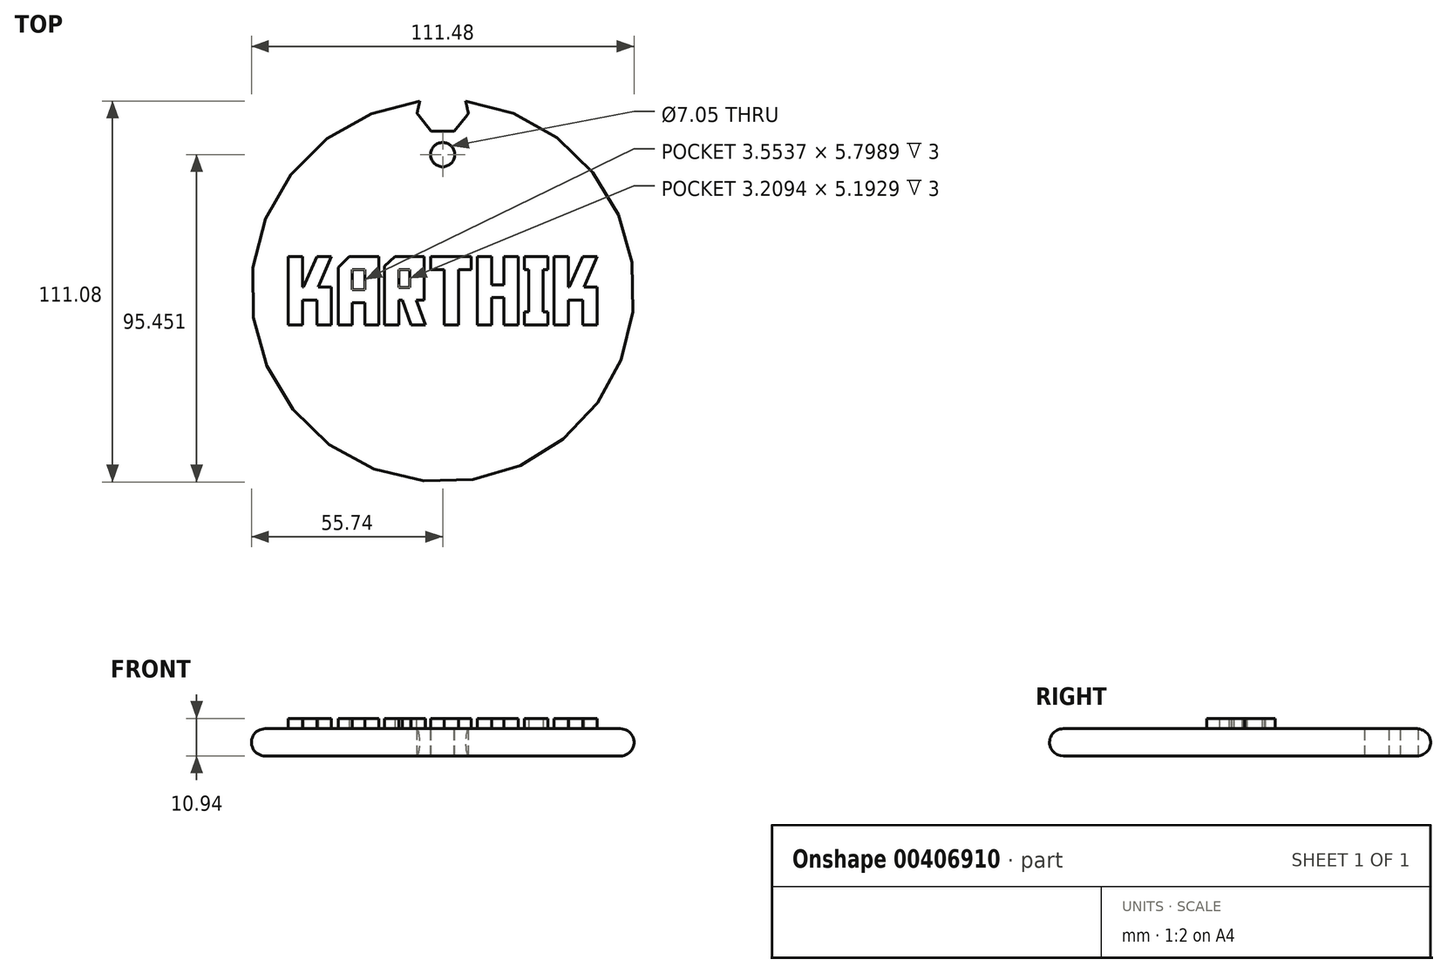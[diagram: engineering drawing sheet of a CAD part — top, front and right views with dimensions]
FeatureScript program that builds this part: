
annotation { "Feature Type Name" : "Feature", "Feature Type Description" : "" }
export const myFeature = defineFeature(function(context is Context, id is Id, definition is map)
    precondition{}
    {
        {
            var Q0;
            Q0=qCreatedBy(makeId("Front.planeOp"),FACE);
            var sketch = newSketch(context, id + "F0", { "sketchPlane" : qUnion([Q0])});
            skLineSegment(sketch, "E0.bottom", {"start": v(0, 0) * mm, "end": v(-51.77, 0) * mm});
            skLineSegment(sketch, "E0.top", {"start": v(0, 7.94) * mm, "end": v(-51.77, 7.94) * mm});
            skLineSegment(sketch, "E0.left", {"start": v(0, 0) * mm, "end": v(0, 7.94) * mm});
            skLineSegment(sketch, "E0.right", {"start": v(-51.77, 0) * mm, "end": v(-51.77, 7.94) * mm});
            skArc(sketch, "E1", {"start": v(-51.77, 7.94) * mm, "mid": v(-55.74, 3.97) * mm, "end": v(-51.77, 0) * mm});
            skSolve(sketch);
        }
        {
            var Q0;
            Q0 = qSketchRegion(id + "F0", true);
            var Q1;
            Q1=sQuery(id+"F0.wireOp",EDGE,"E0.left");
            revolve(context, id + "F1", {"entities" : qUnion([Q0]), "axis" : qUnion([Q1]), "revolveType" : RevolveType.FULL});
        }
        {
            var Q0;
            Q0=makeQuery(id+"F1.opRevolve","SWEPT_FACE",FACE,{"disambiguationData":[OSD([sQuery(id+"F0.wireOp",EDGE,"E0.top")])]});
            var sketch = newSketch(context, id + "F2", { "sketchPlane" : qUnion([Q0])});
            skLineSegment(sketch, "E2", {"start": v(-32.45, 1.07) * mm, "end": v(-32.45, -9.96) * mm});
            skLineSegment(sketch, "E3", {"start": v(-32.45, -9.96) * mm, "end": v(-36.63, -9.96) * mm});
            skLineSegment(sketch, "E4", {"start": v(-36.63, -9.96) * mm, "end": v(-36.63, -2.69) * mm});
            skLineSegment(sketch, "E5", {"start": v(-36.63, -2.69) * mm, "end": v(-40.83, -2.69) * mm});
            skLineSegment(sketch, "E6", {"start": v(-40.83, -2.69) * mm, "end": v(-40.83, -9.96) * mm});
            skLineSegment(sketch, "E7", {"start": v(-40.83, -9.96) * mm, "end": v(-45, -9.96) * mm});
            skLineSegment(sketch, "E8", {"start": v(-45, -9.96) * mm, "end": v(-45, 9.96) * mm});
            skLineSegment(sketch, "E9", {"start": v(-45, 9.96) * mm, "end": v(-40.83, 9.96) * mm});
            skLineSegment(sketch, "E10", {"start": v(-40.83, 9.96) * mm, "end": v(-40.83, 1.07) * mm});
            skLineSegment(sketch, "E11", {"start": v(-40.83, 1.07) * mm, "end": v(-40.55, 1.07) * mm});
            skLineSegment(sketch, "E12", {"start": v(-40.55, 1.07) * mm, "end": v(-36.64, 9.96) * mm});
            skLineSegment(sketch, "E13", {"start": v(-36.64, 9.96) * mm, "end": v(-32.48, 9.96) * mm});
            skLineSegment(sketch, "E14", {"start": v(-32.48, 9.96) * mm, "end": v(-36.3, 1.07) * mm});
            skLineSegment(sketch, "E15", {"start": v(-36.3, 1.07) * mm, "end": v(-32.45, 1.07) * mm});
            skLineSegment(sketch, "E16", {"start": v(-26.3, -9.96) * mm, "end": v(-30.5, -9.96) * mm});
            skLineSegment(sketch, "E17", {"start": v(-30.5, -9.96) * mm, "end": v(-30.5, 6.8) * mm});
            skLineSegment(sketch, "E18", {"start": v(-30.5, 6.8) * mm, "end": v(-27.29, 9.96) * mm});
            skLineSegment(sketch, "E19", {"start": v(-27.29, 9.96) * mm, "end": v(-18.58, 9.96) * mm});
            skLineSegment(sketch, "E20", {"start": v(-18.58, 9.96) * mm, "end": v(-18.58, -9.96) * mm});
            skLineSegment(sketch, "E21", {"start": v(-18.58, -9.96) * mm, "end": v(-22.75, -9.96) * mm});
            skLineSegment(sketch, "E22", {"start": v(-22.75, -9.96) * mm, "end": v(-22.75, -3.42) * mm});
            skLineSegment(sketch, "E23", {"start": v(-22.75, -3.42) * mm, "end": v(-26.3, -3.42) * mm});
            skLineSegment(sketch, "E24", {"start": v(-26.3, -3.42) * mm, "end": v(-26.3, -9.96) * mm});
            skLineSegment(sketch, "E25", {"start": v(-22.75, 0.37) * mm, "end": v(-22.75, 6.17) * mm});
            skLineSegment(sketch, "E26", {"start": v(-22.75, 6.17) * mm, "end": v(-26.3, 6.17) * mm});
            skLineSegment(sketch, "E27", {"start": v(-26.3, 6.17) * mm, "end": v(-26.3, 0.37) * mm});
            skLineSegment(sketch, "E28", {"start": v(-26.3, 0.37) * mm, "end": v(-22.75, 0.37) * mm});
            skLineSegment(sketch, "E29", {"start": v(-9.26, -9.96) * mm, "end": v(-11.74, -2.75) * mm});
            skLineSegment(sketch, "E30", {"start": v(-11.74, -2.75) * mm, "end": v(-12.84, -2.75) * mm});
            skLineSegment(sketch, "E31", {"start": v(-12.84, -2.75) * mm, "end": v(-12.84, -9.96) * mm});
            skLineSegment(sketch, "E32", {"start": v(-12.84, -9.96) * mm, "end": v(-17.01, -9.96) * mm});
            skLineSegment(sketch, "E33", {"start": v(-17.01, -9.96) * mm, "end": v(-17.01, 7.15) * mm});
            skLineSegment(sketch, "E34", {"start": v(-17.01, 7.15) * mm, "end": v(-13.98, 9.96) * mm});
            skLineSegment(sketch, "E35", {"start": v(-13.98, 9.96) * mm, "end": v(-5.45, 9.96) * mm});
            skLineSegment(sketch, "E36", {"start": v(-5.45, 9.96) * mm, "end": v(-5.45, -2.7) * mm});
            skLineSegment(sketch, "E37", {"start": v(-5.45, -2.7) * mm, "end": v(-7.71, -2.7) * mm});
            skLineSegment(sketch, "E38", {"start": v(-7.71, -2.7) * mm, "end": v(-5.07, -9.96) * mm});
            skLineSegment(sketch, "E39", {"start": v(-5.07, -9.96) * mm, "end": v(-9.26, -9.96) * mm});
            skLineSegment(sketch, "E40", {"start": v(-9.63, 0.98) * mm, "end": v(-9.63, 6.17) * mm});
            skLineSegment(sketch, "E41", {"start": v(-9.63, 6.17) * mm, "end": v(-12.84, 6.17) * mm});
            skLineSegment(sketch, "E42", {"start": v(-12.84, 6.17) * mm, "end": v(-12.84, 0.98) * mm});
            skLineSegment(sketch, "E43", {"start": v(-12.84, 0.98) * mm, "end": v(-9.63, 0.98) * mm});
            skLineSegment(sketch, "E44", {"start": v(8.33, 6.17) * mm, "end": v(4.57, 6.17) * mm});
            skLineSegment(sketch, "E45", {"start": v(4.57, 6.17) * mm, "end": v(4.57, -9.96) * mm});
            skLineSegment(sketch, "E46", {"start": v(4.57, -9.96) * mm, "end": v(0.37, -9.96) * mm});
            skLineSegment(sketch, "E47", {"start": v(0.37, -9.96) * mm, "end": v(0.37, 6.17) * mm});
            skLineSegment(sketch, "E48", {"start": v(0.37, 6.17) * mm, "end": v(-3.53, 6.17) * mm});
            skLineSegment(sketch, "E49", {"start": v(-3.53, 6.17) * mm, "end": v(-3.53, 9.96) * mm});
            skLineSegment(sketch, "E50", {"start": v(-3.53, 9.96) * mm, "end": v(8.33, 9.96) * mm});
            skLineSegment(sketch, "E51", {"start": v(8.33, 9.96) * mm, "end": v(8.33, 6.17) * mm});
            skLineSegment(sketch, "E52", {"start": v(14.2, 1.78) * mm, "end": v(17.78, 1.78) * mm});
            skLineSegment(sketch, "E53", {"start": v(17.78, 1.78) * mm, "end": v(17.78, 9.96) * mm});
            skLineSegment(sketch, "E54", {"start": v(17.78, 9.96) * mm, "end": v(21.96, 9.96) * mm});
            skLineSegment(sketch, "E55", {"start": v(21.96, 9.96) * mm, "end": v(21.96, -9.96) * mm});
            skLineSegment(sketch, "E56", {"start": v(21.96, -9.96) * mm, "end": v(17.78, -9.96) * mm});
            skLineSegment(sketch, "E57", {"start": v(17.78, -9.96) * mm, "end": v(17.78, -2) * mm});
            skLineSegment(sketch, "E58", {"start": v(17.78, -2) * mm, "end": v(14.2, -2) * mm});
            skLineSegment(sketch, "E59", {"start": v(14.2, -2) * mm, "end": v(14.2, -9.96) * mm});
            skLineSegment(sketch, "E60", {"start": v(14.2, -9.96) * mm, "end": v(10.03, -9.96) * mm});
            skLineSegment(sketch, "E61", {"start": v(10.03, -9.96) * mm, "end": v(10.03, 9.96) * mm});
            skLineSegment(sketch, "E62", {"start": v(10.03, 9.96) * mm, "end": v(14.2, 9.96) * mm});
            skLineSegment(sketch, "E63", {"start": v(14.2, 9.96) * mm, "end": v(14.2, 1.78) * mm});
            skLineSegment(sketch, "E64", {"start": v(30.66, -6.18) * mm, "end": v(30.66, -9.96) * mm});
            skLineSegment(sketch, "E65", {"start": v(30.66, -9.96) * mm, "end": v(23.73, -9.96) * mm});
            skLineSegment(sketch, "E66", {"start": v(23.73, -9.96) * mm, "end": v(23.73, -6.18) * mm});
            skLineSegment(sketch, "E67", {"start": v(23.73, -6.18) * mm, "end": v(25.11, -6.18) * mm});
            skLineSegment(sketch, "E68", {"start": v(25.11, -6.18) * mm, "end": v(25.11, 6.18) * mm});
            skLineSegment(sketch, "E69", {"start": v(25.11, 6.18) * mm, "end": v(23.73, 6.18) * mm});
            skLineSegment(sketch, "E70", {"start": v(23.73, 6.18) * mm, "end": v(23.73, 9.96) * mm});
            skLineSegment(sketch, "E71", {"start": v(23.73, 9.96) * mm, "end": v(30.66, 9.96) * mm});
            skLineSegment(sketch, "E72", {"start": v(30.66, 9.96) * mm, "end": v(30.66, 6.18) * mm});
            skLineSegment(sketch, "E73", {"start": v(30.66, 6.18) * mm, "end": v(29.28, 6.18) * mm});
            skLineSegment(sketch, "E74", {"start": v(29.28, 6.18) * mm, "end": v(29.28, -6.18) * mm});
            skLineSegment(sketch, "E75", {"start": v(29.28, -6.18) * mm, "end": v(30.66, -6.18) * mm});
            skLineSegment(sketch, "E76", {"start": v(45, 1.07) * mm, "end": v(45, -9.96) * mm});
            skLineSegment(sketch, "E77", {"start": v(45, -9.96) * mm, "end": v(40.83, -9.96) * mm});
            skLineSegment(sketch, "E78", {"start": v(40.83, -9.96) * mm, "end": v(40.83, -2.69) * mm});
            skLineSegment(sketch, "E79", {"start": v(40.83, -2.69) * mm, "end": v(36.63, -2.69) * mm});
            skLineSegment(sketch, "E80", {"start": v(36.63, -2.69) * mm, "end": v(36.63, -9.96) * mm});
            skLineSegment(sketch, "E81", {"start": v(36.63, -9.96) * mm, "end": v(32.45, -9.96) * mm});
            skLineSegment(sketch, "E82", {"start": v(32.45, -9.96) * mm, "end": v(32.45, 9.96) * mm});
            skLineSegment(sketch, "E83", {"start": v(32.45, 9.96) * mm, "end": v(36.63, 9.96) * mm});
            skLineSegment(sketch, "E84", {"start": v(36.63, 9.96) * mm, "end": v(36.63, 1.07) * mm});
            skLineSegment(sketch, "E85", {"start": v(36.63, 1.07) * mm, "end": v(36.9, 1.07) * mm});
            skLineSegment(sketch, "E86", {"start": v(36.9, 1.07) * mm, "end": v(40.81, 9.96) * mm});
            skLineSegment(sketch, "E87", {"start": v(40.81, 9.96) * mm, "end": v(44.97, 9.96) * mm});
            skLineSegment(sketch, "E88", {"start": v(44.97, 9.96) * mm, "end": v(41.16, 1.07) * mm});
            skLineSegment(sketch, "E89", {"start": v(41.16, 1.07) * mm, "end": v(45, 1.07) * mm});
            skSolve(sketch);
        }
        {
            var Q0;
            Q0=makeQuery(id+"F2.imprint","IMPRINT",FACE,{"disambiguationData":[TD([[makeQuery(id+"F2.imprint","IMPRINT",EDGE,{"derivedFrom":sQuery(id+"F2.wireOp",EDGE,"E2")}),1.0]])]});
            var sketch = newSketch(context, id + "F3", { "sketchPlane" : qUnion([Q0])});
            skCircle(sketch, "E90.cCircle", {"center": v(0, 53.46) * mm, "radius": 6.92 * mm, "construction": true});
            skLineSegment(sketch, "E90.0", {"start": v(3.33, 46.54) * mm, "end": v(-3.33, 46.54) * mm});
            skLineSegment(sketch, "E90.1", {"start": v(-3.33, 46.54) * mm, "end": v(-7.49, 51.75) * mm});
            skLineSegment(sketch, "E90.2", {"start": v(-7.49, 51.75) * mm, "end": v(-6, 58.25) * mm});
            skLineSegment(sketch, "E90.3", {"start": v(-6, 58.25) * mm, "end": v(0, 61.14) * mm});
            skLineSegment(sketch, "E90.4", {"start": v(0, 61.14) * mm, "end": v(6, 58.25) * mm});
            skLineSegment(sketch, "E90.5", {"start": v(6, 58.25) * mm, "end": v(7.49, 51.75) * mm});
            skLineSegment(sketch, "E90.6", {"start": v(7.49, 51.75) * mm, "end": v(3.33, 46.54) * mm});
            skPoint(sketch, "E90.0.midPoint", {"position": v(0, 46.54) * mm});
            skSolve(sketch);
        }
        {
            var Q0;
            Q0 = qSketchRegion(id + "F2", true);
            extrude(context, id + "F4", {"entities" : qUnion([Q0]), "operationType" : NewBodyOperationType.ADD, "depth" : 3 * mm});
        }
        {
            var Q0;
            Q0 = qSketchRegion(id + "F3", true);
            extrude(context, id + "F5", {"entities" : qUnion([Q0]), "operationType" : NewBodyOperationType.REMOVE, "oppositeDirection" : true, "depth" : 25.4 * mm});
        }
        {
            var Q0;
            Q0=makeQuery(id+"F4.boolean.opBoolean","SPLIT",FACE,{"disambiguationData":[TD([makeQuery(id+"F1.opRevolve","SWEPT_FACE",FACE,{"disambiguationData":[OSD([sQuery(id+"F0.wireOp",EDGE,"E1")])]})])],"derivedFrom":makeQuery(id+"F1.opRevolve","SWEPT_FACE",FACE,{"disambiguationData":[OSD([sQuery(id+"F0.wireOp",EDGE,"E0.top")])]})});
            var sketch = newSketch(context, id + "F6", { "sketchPlane" : qUnion([Q0])});
            skCircle(sketch, "E91", {"center": v(0, 39.71) * mm, "radius": 3.53 * mm});
            skSolve(sketch);
        }
        {
            var Q0;
            Q0 = qSketchRegion(id + "F6", true);
            extrude(context, id + "F7", {"entities" : qUnion([Q0]), "operationType" : NewBodyOperationType.REMOVE, "oppositeDirection" : true, "depth" : 25.4 * mm});
        }
    });
